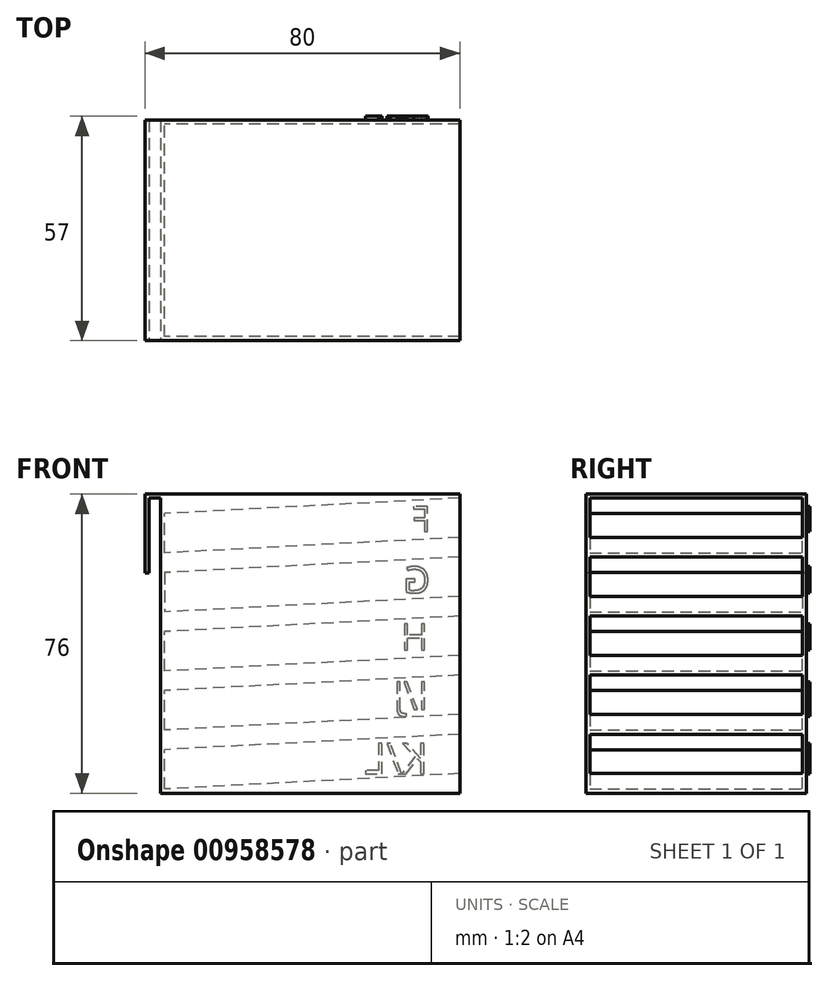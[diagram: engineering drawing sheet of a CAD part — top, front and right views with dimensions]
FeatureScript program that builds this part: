
annotation { "Feature Type Name" : "Feature", "Feature Type Description" : "" }
export const myFeature = defineFeature(function(context is Context, id is Id, definition is map)
    precondition{}
    {
        {
            var Q0;
            Q0=qCreatedBy(makeId("Front.planeOp"),FACE);
            var sketch = newSketch(context, id + "F0", { "sketchPlane" : qUnion([Q0])});
            skLineSegment(sketch, "E0.bottom", {"start": v(38, -38) * mm, "end": v(-38, -38) * mm});
            skLineSegment(sketch, "E0.top", {"start": v(38, 38) * mm, "end": v(-38, 38) * mm});
            skLineSegment(sketch, "E0.left", {"start": v(38, -38) * mm, "end": v(38, 38) * mm});
            skLineSegment(sketch, "E0.right", {"start": v(-38, -38) * mm, "end": v(-38, 38) * mm});
            skPoint(sketch, "E0.middle", {"position": v(0, 0) * mm});
            skSolve(sketch);
        }
        {
            var Q0;
            Q0=makeQuery(id+"F0.imprint","IMPRINT",FACE,{"disambiguationData":[TD([[makeQuery(id+"F0.imprint","IMPRINT",EDGE,{"derivedFrom":sQuery(id+"F0.wireOp",EDGE,"E0.bottom")}),-1.0]])]});
            extrude(context, id + "F1", {"entities" : qUnion([Q0]), "endBound" : BoundingType.SYMMETRIC, "oppositeDirection" : true, "depth" : 56 * mm, "offsetDistance" : 25 * mm});
        }
        {
            var Q0;
            Q0=makeQuery(id+"F1.opExtrude","SWEPT_FACE",FACE,{"disambiguationData":[OSD([sQuery(id+"F0.wireOp",EDGE,"E0.left")])]});
            var sketch = newSketch(context, id + "F2", { "sketchPlane" : qUnion([Q0])});
            skPoint(sketch, "E1", {"position": v(-28, 38) * mm});
            skPoint(sketch, "E2", {"position": v(-28, 37) * mm});
            skPoint(sketch, "E3", {"position": v(-27, 37) * mm});
            skLineSegment(sketch, "E4.bottom", {"start": v(-27, 37) * mm, "end": v(27, 37) * mm});
            skLineSegment(sketch, "E4.top", {"start": v(-27, 27) * mm, "end": v(27, 27) * mm});
            skLineSegment(sketch, "E4.left", {"start": v(-27, 37) * mm, "end": v(-27, 27) * mm});
            skLineSegment(sketch, "E4.right", {"start": v(27, 37) * mm, "end": v(27, 27) * mm});
            skPoint(sketch, "E5", {"position": v(-27, 27) * mm});
            skPoint(sketch, "E6", {"position": v(-27, 22) * mm});
            skLineSegment(sketch, "E7.bottom", {"start": v(-27, 22) * mm, "end": v(27, 22) * mm});
            skLineSegment(sketch, "E7.top", {"start": v(-27, 12) * mm, "end": v(27, 12) * mm});
            skLineSegment(sketch, "E7.left", {"start": v(-27, 22) * mm, "end": v(-27, 12) * mm});
            skLineSegment(sketch, "E7.right", {"start": v(27, 22) * mm, "end": v(27, 12) * mm});
            skPoint(sketch, "E8", {"position": v(-27, 7) * mm});
            skLineSegment(sketch, "E9.bottom", {"start": v(-27, 7) * mm, "end": v(27, 7) * mm});
            skLineSegment(sketch, "E9.top", {"start": v(-27, -3) * mm, "end": v(27, -3) * mm});
            skLineSegment(sketch, "E9.left", {"start": v(-27, 7) * mm, "end": v(-27, -3) * mm});
            skLineSegment(sketch, "E9.right", {"start": v(27, 7) * mm, "end": v(27, -3) * mm});
            skPoint(sketch, "E10", {"position": v(-27, -8) * mm});
            skLineSegment(sketch, "E11.bottom", {"start": v(-27, -8) * mm, "end": v(27, -8) * mm});
            skLineSegment(sketch, "E11.top", {"start": v(-27, -18) * mm, "end": v(27, -18) * mm});
            skLineSegment(sketch, "E11.left", {"start": v(-27, -8) * mm, "end": v(-27, -18) * mm});
            skLineSegment(sketch, "E11.right", {"start": v(27, -8) * mm, "end": v(27, -18) * mm});
            skPoint(sketch, "E12", {"position": v(-27, -23) * mm});
            skLineSegment(sketch, "E13.bottom", {"start": v(-27, -23) * mm, "end": v(27, -23) * mm});
            skLineSegment(sketch, "E13.top", {"start": v(-27, -33) * mm, "end": v(27, -33) * mm});
            skLineSegment(sketch, "E13.left", {"start": v(-27, -23) * mm, "end": v(-27, -33) * mm});
            skLineSegment(sketch, "E13.right", {"start": v(27, -23) * mm, "end": v(27, -33) * mm});
            skSolve(sketch);
        }
        {
            var Q0;
            Q0=makeQuery(id+"F1.opExtrude","CAP_FACE",FACE,{"disambiguationData":[OSD([sQuery(id+"F0.wireOp",EDGE,"E0.bottom"),sQuery(id+"F0.wireOp",EDGE,"E0.top"),sQuery(id+"F0.wireOp",EDGE,"E0.left"),sQuery(id+"F0.wireOp",EDGE,"E0.right")])],"isStart":true});
            var sketch = newSketch(context, id + "F3", { "sketchPlane" : qUnion([Q0])});
            skPoint(sketch, "E14", {"position": v(38, 22) * mm});
            skPoint(sketch, "E15", {"position": v(38, 7) * mm});
            skPoint(sketch, "E16", {"position": v(38, -8) * mm});
            skPoint(sketch, "E17", {"position": v(38, -23) * mm});
            skPoint(sketch, "E18", {"position": v(38, 37) * mm});
            skLineSegment(sketch, "E19", {"start": v(-38, 33.02) * mm, "end": v(-10.2, 33.02) * mm, "construction": true});
            skLineSegment(sketch, "E20", {"start": v(38, 37) * mm, "end": v(-38, 33.02) * mm});
            skLineSegment(sketch, "E21", {"start": v(38, 22) * mm, "end": v(-38, 18.02) * mm});
            skLineSegment(sketch, "E22", {"start": v(-38, 18.02) * mm, "end": v(-8.95, 18.02) * mm, "construction": true});
            skLineSegment(sketch, "E23", {"start": v(38, -23) * mm, "end": v(-38, -26.98) * mm});
            skLineSegment(sketch, "E24", {"start": v(-38, -26.98) * mm, "end": v(-9.06, -26.98) * mm, "construction": true});
            skLineSegment(sketch, "E25", {"start": v(38, 7) * mm, "end": v(-38, 3.02) * mm});
            skLineSegment(sketch, "E26", {"start": v(-38, 3.02) * mm, "end": v(-5.53, 3.02) * mm, "construction": true});
            skLineSegment(sketch, "E27", {"start": v(38, -8) * mm, "end": v(-38, -11.98) * mm});
            skLineSegment(sketch, "E28", {"start": v(-38, -11.98) * mm, "end": v(-6.01, -11.98) * mm});
            skSolve(sketch);
        }
        {
            var Q0;
            Q0=makeQuery(id+"F2.imprint","IMPRINT",FACE,{"disambiguationData":[TD([[makeQuery(id+"F2.imprint","IMPRINT",EDGE,{"derivedFrom":sQuery(id+"F2.wireOp",EDGE,"E4.bottom")}),-1.0]])]});
            var Q1;
            Q1=makeQuery(id+"F2.imprint","IMPRINT",FACE,{"disambiguationData":[TD([[makeQuery(id+"F2.imprint","IMPRINT",EDGE,{"derivedFrom":sQuery(id+"F2.wireOp",EDGE,"E7.bottom")}),-1.0]])]});
            var Q2;
            Q2=makeQuery(id+"F2.imprint","IMPRINT",FACE,{"disambiguationData":[TD([[makeQuery(id+"F2.imprint","IMPRINT",EDGE,{"derivedFrom":sQuery(id+"F2.wireOp",EDGE,"E9.bottom")}),-1.0]])]});
            var Q3;
            Q3=makeQuery(id+"F2.imprint","IMPRINT",FACE,{"disambiguationData":[TD([[makeQuery(id+"F2.imprint","IMPRINT",EDGE,{"derivedFrom":sQuery(id+"F2.wireOp",EDGE,"E11.bottom")}),-1.0]])]});
            var Q4;
            Q4=makeQuery(id+"F2.imprint","IMPRINT",FACE,{"disambiguationData":[TD([[makeQuery(id+"F2.imprint","IMPRINT",EDGE,{"derivedFrom":sQuery(id+"F2.wireOp",EDGE,"E13.bottom")}),-1.0]])]});
            var Q5;
            Q5=sQuery(id+"F3.wireOp",EDGE,"E20");
            sweep(context, id + "F4", {"operationType" : NewBodyOperationType.REMOVE, "profiles" : qUnion([Q0, Q1, Q2, Q3, Q4]), "path" : qUnion([Q5])});
        }
        {
            var Q0;
            Q0=makeQuery(id+"F1.opExtrude","SWEPT_FACE",FACE,{"disambiguationData":[OSD([sQuery(id+"F0.wireOp",EDGE,"E0.right")])]});
            var sketch = newSketch(context, id + "F5", { "sketchPlane" : qUnion([Q0])});
            skLineSegment(sketch, "E29.bottom", {"start": v(-28, 38) * mm, "end": v(28, 38) * mm});
            skLineSegment(sketch, "E29.top", {"start": v(-28, -38) * mm, "end": v(28, -38) * mm});
            skLineSegment(sketch, "E29.left", {"start": v(-28, 38) * mm, "end": v(-28, -38) * mm});
            skLineSegment(sketch, "E29.right", {"start": v(28, 38) * mm, "end": v(28, -38) * mm});
            skSolve(sketch);
        }
        {
            var Q0;
            Q0=qSketchRegion(id+"F5",true);
            extrude(context, id + "F6", {"entities" : qUnion([Q0]), "operationType" : NewBodyOperationType.ADD, "oppositeDirection" : true, "depth" : 1 * mm, "offsetDistance" : 25 * mm});
        }
        {
            var Q0;
            Q0=makeQuery(id+"F1.opExtrude","CAP_FACE",FACE,{"disambiguationData":[OSD([sQuery(id+"F0.wireOp",EDGE,"E0.bottom"),sQuery(id+"F0.wireOp",EDGE,"E0.top"),sQuery(id+"F0.wireOp",EDGE,"E0.left"),sQuery(id+"F0.wireOp",EDGE,"E0.right")])],"isStart":true});
            var sketch = newSketch(context, id + "F7", { "sketchPlane" : qUnion([Q0])});
            skLineSegment(sketch, "E30", {"start": v(-38, 38) * mm, "end": v(-42, 38) * mm});
            skLineSegment(sketch, "E31", {"start": v(-42, 38) * mm, "end": v(-42, 18) * mm});
            skLineSegment(sketch, "E32", {"start": v(-42, 18) * mm, "end": v(-41, 18) * mm});
            skLineSegment(sketch, "E33", {"start": v(-41, 18) * mm, "end": v(-41, 37) * mm});
            skLineSegment(sketch, "E34", {"start": v(-41, 37) * mm, "end": v(-38, 37) * mm});
            skSolve(sketch);
        }
        {
            var Q0;
            {var subQ0=sQuery(id+"F7.wireOp",EDGE,"E30");Q0=makeQuery(id+"F7.imprint","IMPRINT",FACE,{"disambiguationData":[TD([[makeQuery(id+"F7.imprint","IMPRINT",EDGE,{"derivedFrom":subQ0}),1.0]])]});}
            extrude(context, id + "F8", {"entities" : qUnion([Q0]), "operationType" : NewBodyOperationType.ADD, "oppositeDirection" : true, "depth" : 56 * mm, "offsetDistance" : 25 * mm});
        }
        {
            var Q0;
            {var subQ0=sQuery(id+"F0.wireOp",EDGE,"E0.right");Q0=makeQuery(id+"F8.boolean.opBoolean","MERGE",FACE,{"derivedFrom":[makeQuery(id+"F1.opExtrude","CAP_FACE",FACE,{"disambiguationData":[OSD([sQuery(id+"F0.wireOp",EDGE,"E0.bottom"),sQuery(id+"F0.wireOp",EDGE,"E0.top"),sQuery(id+"F0.wireOp",EDGE,"E0.left"),subQ0])],"isStart":false}),makeQuery(id+"F8.opExtrude","CAP_FACE",FACE,{"disambiguationData":[OSD([subQ0,sQuery(id+"F7.wireOp",EDGE,"E30"),sQuery(id+"F7.wireOp",EDGE,"E31"),sQuery(id+"F7.wireOp",EDGE,"E32"),sQuery(id+"F7.wireOp",EDGE,"E33"),sQuery(id+"F7.wireOp",EDGE,"E34")])],"isStart":false})]});}
            var sketch = newSketch(context, id + "F9", { "sketchPlane" : qUnion([Q0])});
            skText(sketch, "E35", { "text": "F", "fontName": "OpenSans-Regular.ttf"});
            skText(sketch, "E36", { "text": "G", "fontName": "OpenSans-Regular.ttf"});
            skText(sketch, "E37", { "text": "H", "fontName": "OpenSans-Regular.ttf"});
            skText(sketch, "E38", { "text": "I/J", "fontName": "OpenSans-Regular.ttf"});
            skText(sketch, "E39", { "text": "K/L", "fontName": "OpenSans-Regular.ttf"});
            const initialGuessF9  = {"E35": [-0.03067, 0.02852, 1, 0, 0.00643], "E36": [-0.03044, 0.01292, 1, 0, 0.00667], "E37": [-0.02997, -0.00164, 1, 0, 0.00676], "E38": [-0.02997, -0.01666, 1, 0, 0.00695], "E39": [-0.02997, -0.03303, 1, 0, 0.0078]};
            skSetInitialGuess(sketch, initialGuessF9);
            skSolve(sketch);
        }
        {
            var Q0;
            Q0=qSketchRegion(id+"F9",true);
            extrude(context, id + "F10", {"entities" : qUnion([Q0]), "operationType" : NewBodyOperationType.ADD, "depth" : 1 * mm, "offsetDistance" : 25 * mm});
        }
    });
